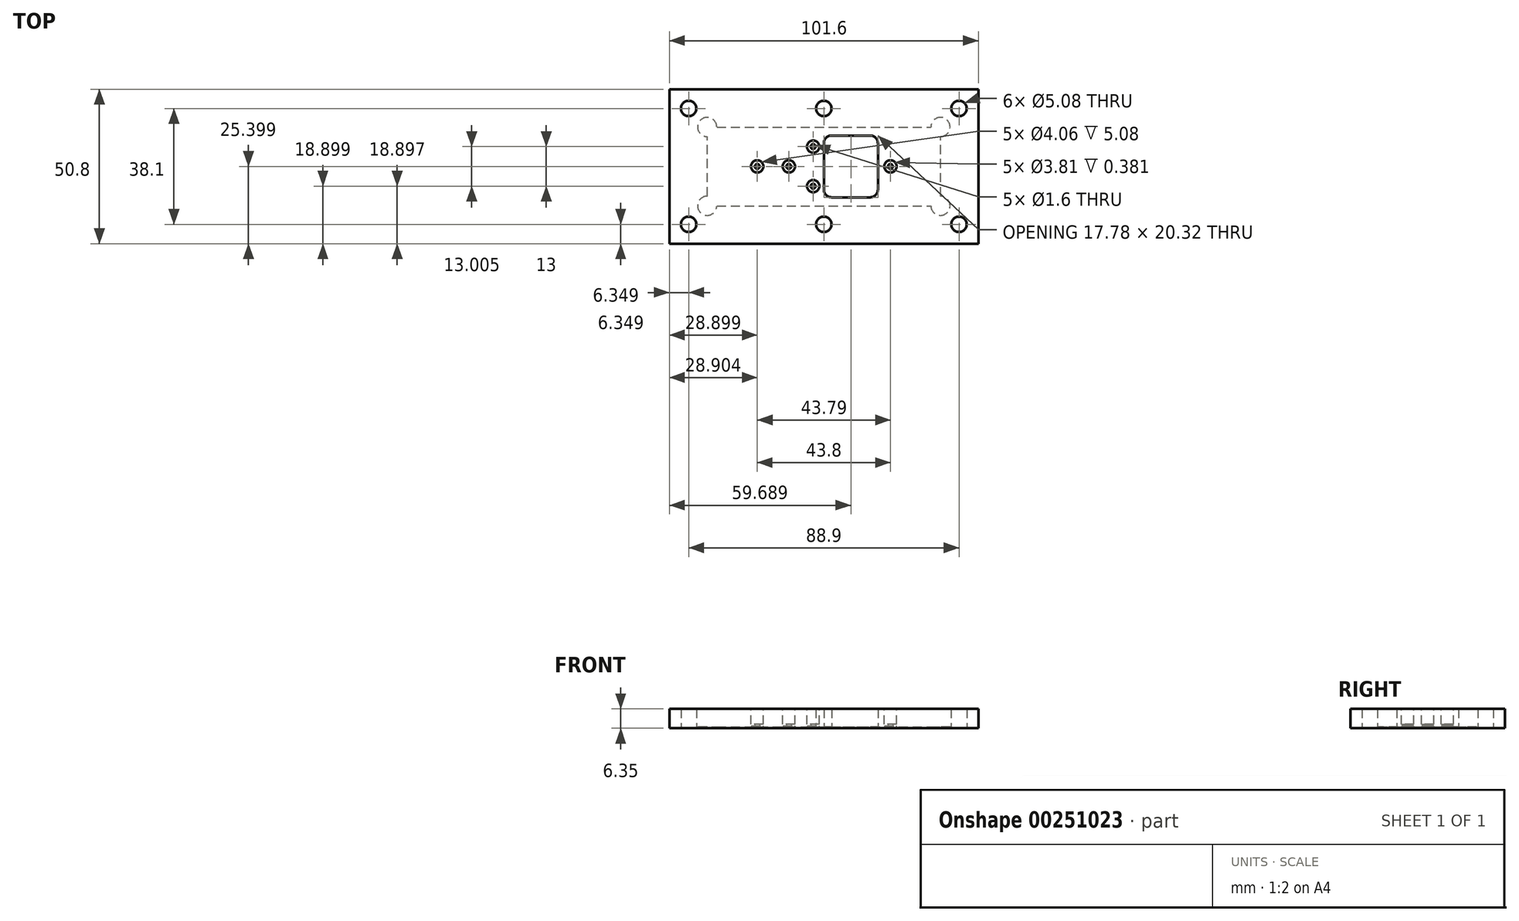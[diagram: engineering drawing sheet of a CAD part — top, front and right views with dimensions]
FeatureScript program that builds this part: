
annotation { "Feature Type Name" : "Feature", "Feature Type Description" : "" }
export const myFeature = defineFeature(function(context is Context, id is Id, definition is map)
    precondition{}
    {
        {
            var Q0;
            Q0=qCreatedBy(makeId("Top.planeOp"),FACE);
            var sketch = newSketch(context, id + "F0", { "sketchPlane" : qUnion([Q0])});
            skLineSegment(sketch, "E0.bottom", {"start": v(-51.27, 22.54) * mm, "end": v(50.33, 22.54) * mm});
            skLineSegment(sketch, "E0.top", {"start": v(-51.27, -28.26) * mm, "end": v(50.33, -28.26) * mm});
            skLineSegment(sketch, "E0.left", {"start": v(-51.27, 22.54) * mm, "end": v(-51.27, -28.26) * mm});
            skLineSegment(sketch, "E0.right", {"start": v(50.33, 22.54) * mm, "end": v(50.33, -28.26) * mm});
            skSolve(sketch);
        }
        {
            var Q0;
            Q0=makeQuery(id+"F0.imprint","IMPRINT",FACE,{"disambiguationData":[TD([[makeQuery(id+"F0.imprint","IMPRINT",EDGE,{"derivedFrom":sQuery(id+"F0.wireOp",EDGE,"E0.bottom")}),-1.0]])]});
            extrude(context, id + "F1", {"entities" : qUnion([Q0]), "depth" : 6.35 * mm});
        }
        {
            var Q0;
            Q0=makeQuery(id+"F1.opExtrude","CAP_FACE",FACE,{"disambiguationData":[OSD([sQuery(id+"F0.wireOp",EDGE,"E0.bottom"),sQuery(id+"F0.wireOp",EDGE,"E0.top"),sQuery(id+"F0.wireOp",EDGE,"E0.left"),sQuery(id+"F0.wireOp",EDGE,"E0.right")])],"isStart":true});
            var sketch = newSketch(context, id + "F2", { "sketchPlane" : qUnion([Q0])});
            skLineSegment(sketch, "E1.bottom", {"start": v(-38.83, 15.82) * mm, "end": v(37.88, 15.82) * mm});
            skLineSegment(sketch, "E1.top", {"start": v(-38.83, -10.1) * mm, "end": v(37.88, -10.1) * mm});
            skLineSegment(sketch, "E1.left", {"start": v(-38.83, 15.82) * mm, "end": v(-38.83, -10.1) * mm});
            skLineSegment(sketch, "E1.right", {"start": v(37.88, 15.82) * mm, "end": v(37.88, -10.1) * mm});
            skCircle(sketch, "E2", {"center": v(-38.83, 15.82) * mm, "radius": 3.18 * mm});
            skCircle(sketch, "E3", {"center": v(37.88, 15.82) * mm, "radius": 3.18 * mm});
            skCircle(sketch, "E4", {"center": v(37.88, -10.1) * mm, "radius": 3.18 * mm});
            skCircle(sketch, "E5", {"center": v(-38.83, -10.1) * mm, "radius": 3.18 * mm});
            skSolve(sketch);
        }
        {
            var Q0;
            {var subQ0=sQuery(id+"F2.wireOp",EDGE,"E1.left");var subQ1=sQuery(id+"F2.wireOp",EDGE,"E1.top");var subQ2=makeQuery(id+"F2.imprint","INTERSECT",VERTEX,{"derivedFrom":[subQ1,subQ0]});Q0=makeQuery(id+"F2.imprint","IMPRINT",FACE,{"disambiguationData":[TD([[makeQuery(id+"F2.imprint","IMPRINT",EDGE,{"disambiguationData":[TD([[subQ2,-1.0]])],"derivedFrom":subQ1}),-1.0]])]});}
            var Q1;
            {var subQ0=sQuery(id+"F2.wireOp",EDGE,"E1.right");var subQ1=sQuery(id+"F2.wireOp",EDGE,"E1.top");var subQ2=makeQuery(id+"F2.imprint","INTERSECT",VERTEX,{"derivedFrom":[subQ1,subQ0]});Q1=makeQuery(id+"F2.imprint","IMPRINT",FACE,{"disambiguationData":[TD([[makeQuery(id+"F2.imprint","IMPRINT",EDGE,{"disambiguationData":[TD([[subQ2,1.0]])],"derivedFrom":subQ1}),1.0]])]});}
            var Q2;
            {var subQ0=sQuery(id+"F2.wireOp",EDGE,"E1.right");var subQ1=sQuery(id+"F2.wireOp",EDGE,"E1.top");var subQ2=makeQuery(id+"F2.imprint","INTERSECT",VERTEX,{"derivedFrom":[subQ1,subQ0]});Q2=makeQuery(id+"F2.imprint","IMPRINT",FACE,{"disambiguationData":[TD([[makeQuery(id+"F2.imprint","IMPRINT",EDGE,{"disambiguationData":[TD([[subQ2,1.0]])],"derivedFrom":subQ1}),-1.0]])]});}
            var Q3;
            {var subQ0=sQuery(id+"F2.wireOp",EDGE,"E2");var subQ13=sQuery(id+"F2.wireOp",EDGE,"E1.bottom");var subQ14=makeQuery(id+"F2.imprint","INTERSECT",VERTEX,{"derivedFrom":[subQ13,subQ0]});Q3=makeQuery(id+"F2.imprint","IMPRINT",FACE,{"disambiguationData":[TD([[makeQuery(id+"F2.imprint","IMPRINT",EDGE,{"disambiguationData":[TD([[subQ14,-1.0]])],"derivedFrom":subQ13}),-1.0]])]});}
            var Q4;
            {var subQ0=sQuery(id+"F2.wireOp",EDGE,"E1.left");var subQ1=sQuery(id+"F2.wireOp",EDGE,"E1.top");var subQ2=makeQuery(id+"F2.imprint","INTERSECT",VERTEX,{"derivedFrom":[subQ1,subQ0]});Q4=makeQuery(id+"F2.imprint","IMPRINT",FACE,{"disambiguationData":[TD([[makeQuery(id+"F2.imprint","IMPRINT",EDGE,{"disambiguationData":[TD([[subQ2,-1.0]])],"derivedFrom":subQ1}),1.0]])]});}
            var Q5;
            {var subQ0=sQuery(id+"F2.wireOp",EDGE,"E1.right");var subQ1=sQuery(id+"F2.wireOp",EDGE,"E1.bottom");var subQ2=makeQuery(id+"F2.imprint","INTERSECT",VERTEX,{"derivedFrom":[subQ1,subQ0]});Q5=makeQuery(id+"F2.imprint","IMPRINT",FACE,{"disambiguationData":[TD([[makeQuery(id+"F2.imprint","IMPRINT",EDGE,{"disambiguationData":[TD([[subQ2,1.0]])],"derivedFrom":subQ1}),1.0]])]});}
            var Q6;
            {var subQ0=sQuery(id+"F2.wireOp",EDGE,"E1.right");var subQ1=sQuery(id+"F2.wireOp",EDGE,"E1.bottom");var subQ2=makeQuery(id+"F2.imprint","INTERSECT",VERTEX,{"derivedFrom":[subQ1,subQ0]});Q6=makeQuery(id+"F2.imprint","IMPRINT",FACE,{"disambiguationData":[TD([[makeQuery(id+"F2.imprint","IMPRINT",EDGE,{"disambiguationData":[TD([[subQ2,1.0]])],"derivedFrom":subQ1}),-1.0]])]});}
            var Q7;
            {var subQ0=sQuery(id+"F2.wireOp",EDGE,"E1.left");var subQ1=sQuery(id+"F2.wireOp",EDGE,"E1.bottom");var subQ2=makeQuery(id+"F2.imprint","INTERSECT",VERTEX,{"derivedFrom":[subQ1,subQ0]});Q7=makeQuery(id+"F2.imprint","IMPRINT",FACE,{"disambiguationData":[TD([[makeQuery(id+"F2.imprint","IMPRINT",EDGE,{"disambiguationData":[TD([[subQ2,-1.0]])],"derivedFrom":subQ1}),-1.0]])]});}
            var Q8;
            {var subQ0=sQuery(id+"F2.wireOp",EDGE,"E1.left");var subQ1=sQuery(id+"F2.wireOp",EDGE,"E1.bottom");var subQ2=makeQuery(id+"F2.imprint","INTERSECT",VERTEX,{"derivedFrom":[subQ1,subQ0]});Q8=makeQuery(id+"F2.imprint","IMPRINT",FACE,{"disambiguationData":[TD([[makeQuery(id+"F2.imprint","IMPRINT",EDGE,{"disambiguationData":[TD([[subQ2,-1.0]])],"derivedFrom":subQ1}),1.0]])]});}
            extrude(context, id + "F3", {"entities" : qUnion([Q0, Q1, Q2, Q3, Q4, Q5, Q6, Q7, Q8]), "operationType" : NewBodyOperationType.REMOVE, "oppositeDirection" : true, "depth" : 0.38 * mm});
        }
        {
            var Q0;
            Q0=makeQuery(id+"F3.boolean.opBoolean","COPY",FACE,{"derivedFrom":makeQuery(id+"F3.opExtrude","CAP_FACE",FACE,{"disambiguationData":[OSD([sQuery(id+"F2.wireOp",EDGE,"E1.bottom"),sQuery(id+"F2.wireOp",EDGE,"E1.top"),sQuery(id+"F2.wireOp",EDGE,"E1.left"),sQuery(id+"F2.wireOp",EDGE,"E1.right"),sQuery(id+"F2.wireOp",EDGE,"E2"),sQuery(id+"F2.wireOp",EDGE,"E3"),sQuery(id+"F2.wireOp",EDGE,"E4"),sQuery(id+"F2.wireOp",EDGE,"E5")])],"isStart":false})});
            var sketch = newSketch(context, id + "F4", { "sketchPlane" : qUnion([Q0])});
            skLineSegment(sketch, "E6.bottom", {"start": v(2.07, 13.02) * mm, "end": v(14.77, 13.02) * mm});
            skLineSegment(sketch, "E6.top", {"start": v(2.07, -7.3) * mm, "end": v(14.77, -7.3) * mm});
            skLineSegment(sketch, "E6.left", {"start": v(-0.47, 10.48) * mm, "end": v(-0.47, -4.76) * mm});
            skLineSegment(sketch, "E6.right", {"start": v(17.3, 10.48) * mm, "end": v(17.3, -4.76) * mm});
            skPoint(sketch, "E7.visualSharp", {"position": v(-0.47, 13.02) * mm});
            skArc(sketch, "E7.filletArc", {"start": v(2.07, 13.02) * mm, "mid": v(0.27, 12.28) * mm, "end": v(-0.47, 10.48) * mm});
            skPoint(sketch, "E8.visualSharp", {"position": v(-0.47, -7.3) * mm});
            skArc(sketch, "E8.filletArc", {"start": v(-0.47, -4.76) * mm, "mid": v(0.27, -6.56) * mm, "end": v(2.07, -7.3) * mm});
            skPoint(sketch, "E9.visualSharp", {"position": v(17.3, -7.3) * mm});
            skArc(sketch, "E9.filletArc", {"start": v(14.77, -7.3) * mm, "mid": v(16.56, -6.56) * mm, "end": v(17.3, -4.76) * mm});
            skPoint(sketch, "E10.visualSharp", {"position": v(17.3, 13.02) * mm});
            skArc(sketch, "E10.filletArc", {"start": v(17.3, 10.48) * mm, "mid": v(16.56, 12.28) * mm, "end": v(14.77, 13.02) * mm});
            skSolve(sketch);
        }
        {
            var Q0;
            Q0 = qSketchRegion(id + "F4", true);
            extrude(context, id + "F5", {"entities" : qUnion([Q0]), "operationType" : NewBodyOperationType.REMOVE, "endBound" : BoundingType.UP_TO_NEXT, "oppositeDirection" : true, "depth" : 25.4 * mm});
        }
        {
            var Q0;
            Q0=makeQuery(id+"F1.opExtrude","CAP_FACE",FACE,{"disambiguationData":[OSD([sQuery(id+"F0.wireOp",EDGE,"E0.bottom"),sQuery(id+"F0.wireOp",EDGE,"E0.top"),sQuery(id+"F0.wireOp",EDGE,"E0.left"),sQuery(id+"F0.wireOp",EDGE,"E0.right")])],"isStart":true});
            var sketch = newSketch(context, id + "F6", { "sketchPlane" : qUnion([Q0])});
            skCircle(sketch, "E11", {"center": v(-44.92, 21.91) * mm, "radius": 2.54 * mm});
            skCircle(sketch, "E12", {"center": v(43.98, 21.91) * mm, "radius": 2.54 * mm});
            skCircle(sketch, "E13", {"center": v(43.98, -16.19) * mm, "radius": 2.54 * mm});
            skCircle(sketch, "E14", {"center": v(-0.47, -16.19) * mm, "radius": 2.54 * mm});
            skCircle(sketch, "E15", {"center": v(-44.92, -16.19) * mm, "radius": 2.54 * mm});
            skCircle(sketch, "E16", {"center": v(-0.47, 21.91) * mm, "radius": 2.54 * mm});
            skSolve(sketch);
        }
        {
            var Q0;
            Q0 = qSketchRegion(id + "F6", true);
            extrude(context, id + "F7", {"entities" : qUnion([Q0]), "operationType" : NewBodyOperationType.REMOVE, "endBound" : BoundingType.UP_TO_NEXT, "oppositeDirection" : true, "depth" : 25.4 * mm});
        }
        {
            var Q0;
            Q0=makeQuery(id+"F1.opExtrude","CAP_FACE",FACE,{"disambiguationData":[OSD([sQuery(id+"F0.wireOp",EDGE,"E0.bottom"),sQuery(id+"F0.wireOp",EDGE,"E0.top"),sQuery(id+"F0.wireOp",EDGE,"E0.left"),sQuery(id+"F0.wireOp",EDGE,"E0.right")])],"isStart":false});
            var sketch = newSketch(context, id + "F8", { "sketchPlane" : qUnion([Q0])});
            skCircle(sketch, "E17", {"center": v(-22.37, -2.86) * mm, "radius": 2.03 * mm});
            skCircle(sketch, "E18", {"center": v(-11.97, -2.86) * mm, "radius": 2.03 * mm});
            skCircle(sketch, "E19", {"center": v(-3.97, 3.64) * mm, "radius": 2.03 * mm});
            skCircle(sketch, "E20", {"center": v(-3.97, -9.36) * mm, "radius": 2.03 * mm});
            skCircle(sketch, "E21", {"center": v(21.43, -2.86) * mm, "radius": 2.03 * mm});
            skSolve(sketch);
        }
        {
            var Q0;
            Q0 = qSketchRegion(id + "F8", true);
            extrude(context, id + "F9", {"entities" : qUnion([Q0]), "operationType" : NewBodyOperationType.REMOVE, "oppositeDirection" : true, "depth" : 5.08 * mm});
        }
        {
            var Q0;
            Q0=makeQuery(id+"F3.boolean.opBoolean","COPY",FACE,{"derivedFrom":makeQuery(id+"F3.opExtrude","CAP_FACE",FACE,{"disambiguationData":[OSD([sQuery(id+"F2.wireOp",EDGE,"E1.bottom"),sQuery(id+"F2.wireOp",EDGE,"E1.top"),sQuery(id+"F2.wireOp",EDGE,"E1.left"),sQuery(id+"F2.wireOp",EDGE,"E1.right"),sQuery(id+"F2.wireOp",EDGE,"E2"),sQuery(id+"F2.wireOp",EDGE,"E3"),sQuery(id+"F2.wireOp",EDGE,"E4"),sQuery(id+"F2.wireOp",EDGE,"E5")])],"isStart":false})});
            var sketch = newSketch(context, id + "F10", { "sketchPlane" : qUnion([Q0])});
            skCircle(sketch, "E22", {"center": v(-22.37, 2.86) * mm, "radius": 1.9 * mm});
            skCircle(sketch, "E23", {"center": v(-11.98, 2.86) * mm, "radius": 1.9 * mm});
            skCircle(sketch, "E24", {"center": v(-3.98, 9.36) * mm, "radius": 1.9 * mm});
            skCircle(sketch, "E25", {"center": v(-3.98, -3.64) * mm, "radius": 1.9 * mm});
            skCircle(sketch, "E26", {"center": v(21.42, 2.86) * mm, "radius": 1.9 * mm});
            skSolve(sketch);
        }
        {
            var Q0;
            Q0 = qSketchRegion(id + "F10", true);
            extrude(context, id + "F11", {"entities" : qUnion([Q0]), "operationType" : NewBodyOperationType.REMOVE, "oppositeDirection" : true, "depth" : 0.38 * mm});
        }
        {
            var Q0;
            Q0=makeQuery(id+"F11.boolean.opBoolean","COPY",FACE,{"derivedFrom":makeQuery(id+"F11.opExtrude","CAP_FACE",FACE,{"disambiguationData":[OSD([sQuery(id+"F10.wireOp",EDGE,"E22")])],"isStart":false})});
            var sketch = newSketch(context, id + "F12", { "sketchPlane" : qUnion([Q0])});
            skCircle(sketch, "E27", {"center": v(-22.37, 2.86) * mm, "radius": 0.8 * mm});
            skCircle(sketch, "E28", {"center": v(-11.98, 2.86) * mm, "radius": 0.8 * mm});
            skCircle(sketch, "E29", {"center": v(-3.98, 9.36) * mm, "radius": 0.8 * mm});
            skCircle(sketch, "E30", {"center": v(-3.98, -3.64) * mm, "radius": 0.8 * mm});
            skCircle(sketch, "E31", {"center": v(21.42, 2.86) * mm, "radius": 0.8 * mm});
            skSolve(sketch);
        }
        {
            var Q0;
            Q0 = qSketchRegion(id + "F12", true);
            extrude(context, id + "F13", {"entities" : qUnion([Q0]), "operationType" : NewBodyOperationType.REMOVE, "endBound" : BoundingType.UP_TO_NEXT, "oppositeDirection" : true, "depth" : 25.4 * mm});
        }
    });
